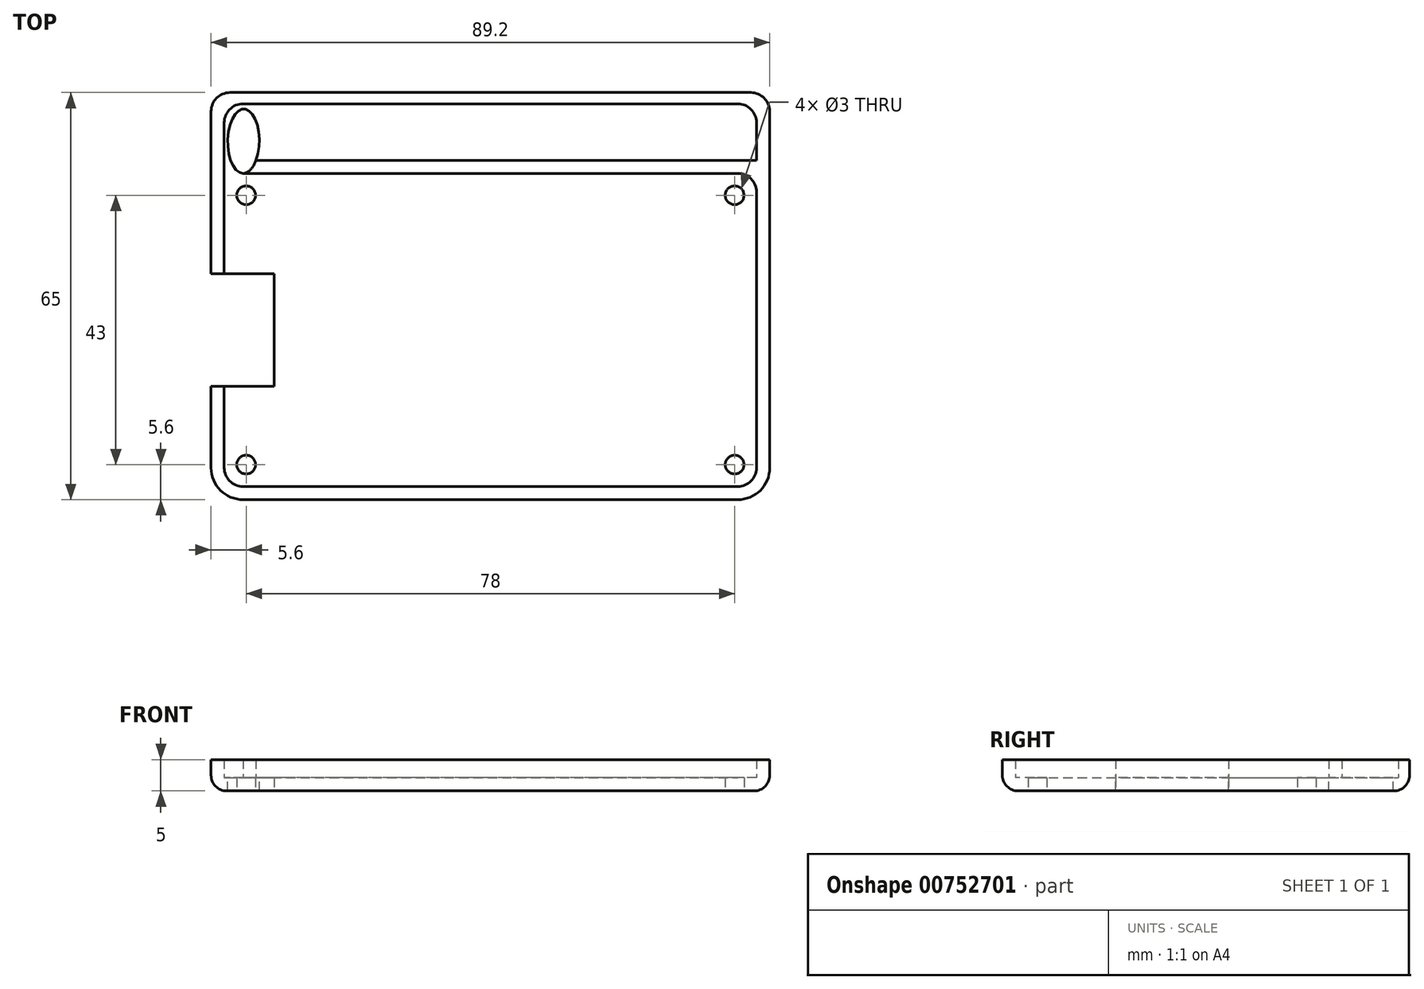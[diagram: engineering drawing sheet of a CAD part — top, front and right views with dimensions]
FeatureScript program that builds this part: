
annotation { "Feature Type Name" : "Feature", "Feature Type Description" : "" }
export const myFeature = defineFeature(function(context is Context, id is Id, definition is map)
    precondition{}
    {
        {
            var Q0;
            Q0=qCreatedBy(makeId("Top.planeOp"),FACE);
            var sketch = newSketch(context, id + "F0", { "sketchPlane" : qUnion([Q0])});
            skLineSegment(sketch, "E0.bottom", {"start": v(-39.5, 25) * mm, "end": v(39.5, 25) * mm});
            skLineSegment(sketch, "E0.top", {"start": v(-39.5, -25) * mm, "end": v(39.5, -25) * mm});
            skLineSegment(sketch, "E0.left", {"start": v(-42.5, 22) * mm, "end": v(-42.5, -22) * mm});
            skLineSegment(sketch, "E0.right", {"start": v(42.5, 22) * mm, "end": v(42.5, -22) * mm});
            skPoint(sketch, "E0.middle", {"position": v(0, 0) * mm});
            skLineSegment(sketch, "E1.bottom", {"start": v(-39, 21.5) * mm, "end": v(39, 21.5) * mm, "construction": true});
            skLineSegment(sketch, "E1.top", {"start": v(-39, -21.5) * mm, "end": v(39, -21.5) * mm, "construction": true});
            skLineSegment(sketch, "E1.left", {"start": v(-39, 21.5) * mm, "end": v(-39, -21.5) * mm, "construction": true});
            skLineSegment(sketch, "E1.right", {"start": v(39, 21.5) * mm, "end": v(39, -21.5) * mm, "construction": true});
            skCircle(sketch, "E2", {"center": v(-39, 21.5) * mm, "radius": 1.5 * mm});
            skCircle(sketch, "E3", {"center": v(39, 21.5) * mm, "radius": 1.5 * mm});
            skCircle(sketch, "E4", {"center": v(39, -21.5) * mm, "radius": 1.5 * mm});
            skCircle(sketch, "E5", {"center": v(-39, -21.5) * mm, "radius": 1.5 * mm});
            skPoint(sketch, "E6.visualSharp", {"position": v(-42.5, 25) * mm});
            skArc(sketch, "E6.filletArc", {"start": v(-39.5, 25) * mm, "mid": v(-41.62, 24.12) * mm, "end": v(-42.5, 22) * mm});
            skPoint(sketch, "E7.visualSharp", {"position": v(42.5, 25) * mm});
            skArc(sketch, "E7.filletArc", {"start": v(42.5, 22) * mm, "mid": v(41.62, 24.12) * mm, "end": v(39.5, 25) * mm});
            skPoint(sketch, "E8.visualSharp", {"position": v(42.5, -25) * mm});
            skArc(sketch, "E8.filletArc", {"start": v(39.5, -25) * mm, "mid": v(41.62, -24.12) * mm, "end": v(42.5, -22) * mm});
            skPoint(sketch, "E9.visualSharp", {"position": v(-42.5, -25) * mm});
            skArc(sketch, "E9.filletArc", {"start": v(-42.5, -22) * mm, "mid": v(-41.62, -24.12) * mm, "end": v(-39.5, -25) * mm});
            skLineSegment(sketch, "E10", {"start": v(0, 0) * mm, "end": v(-34.5, 0) * mm, "construction": true});
            skLineSegment(sketch, "E11", {"start": v(-34.5, 25) * mm, "end": v(-34.5, -25) * mm});
            skLineSegment(sketch, "E12", {"start": v(0, 0) * mm, "end": v(0, 9.32) * mm, "construction": true});
            skLineSegment(sketch, "E13.MirrorCS", {"start": v(34.5, 25) * mm, "end": v(34.5, -25) * mm});
            skLineSegment(sketch, "E14.1", {"start": v(-44.6, 22) * mm, "end": v(-44.6, -22) * mm});
            skLineSegment(sketch, "E14.2", {"start": v(-39.5, 27.1) * mm, "end": v(39.5, 27.1) * mm});
            skArc(sketch, "E14.3", {"start": v(-44.6, -22) * mm, "mid": v(-43.1, -25.6) * mm, "end": v(-39.5, -27.1) * mm});
            skLineSegment(sketch, "E14.5", {"start": v(44.6, 22) * mm, "end": v(44.6, -22) * mm});
            skArc(sketch, "E14.6", {"start": v(39.5, -27.1) * mm, "mid": v(43.1, -25.6) * mm, "end": v(44.6, -22) * mm});
            skLineSegment(sketch, "E14.7", {"start": v(-39.5, -27.1) * mm, "end": v(39.5, -27.1) * mm});
            skLineSegment(sketch, "E15", {"start": v(-42.5, 0) * mm, "end": v(-44.6, 0) * mm, "construction": true});
            skLineSegment(sketch, "E16.bottom", {"start": v(-44.6, 9) * mm, "end": v(-42.5, 9) * mm});
            skLineSegment(sketch, "E16.top", {"start": v(-44.6, -9) * mm, "end": v(-42.5, -9) * mm});
            skLineSegment(sketch, "E16.left", {"start": v(-44.6, 9) * mm, "end": v(-44.6, -9) * mm});
            skLineSegment(sketch, "E16.right", {"start": v(-42.5, 9) * mm, "end": v(-42.5, -9) * mm});
            skPoint(sketch, "E16.middle", {"position": v(-43.55, 0) * mm});
            skLineSegment(sketch, "E17", {"start": v(-42.5, 9) * mm, "end": v(-34.5, 9) * mm});
            skLineSegment(sketch, "E18", {"start": v(-42.5, -9) * mm, "end": v(-34.5, -9) * mm});
            skLineSegment(sketch, "E19", {"start": v(0, 27.1) * mm, "end": v(0, 36.1) * mm, "construction": true});
            skLineSegment(sketch, "E20", {"start": v(0, 36.1) * mm, "end": v(-39.5, 36.1) * mm});
            skLineSegment(sketch, "E21", {"start": v(0, 36.1) * mm, "end": v(39.5, 36.1) * mm});
            skLineSegment(sketch, "E22.0", {"start": v(0, 37.9) * mm, "end": v(41.6, 37.9) * mm});
            skLineSegment(sketch, "E22.1", {"start": v(0, 37.9) * mm, "end": v(-41.6, 37.9) * mm});
            skLineSegment(sketch, "E23", {"start": v(-42.5, 22) * mm, "end": v(-42.5, 33.1) * mm});
            skLineSegment(sketch, "E24", {"start": v(42.5, 22) * mm, "end": v(42.5, 33.1) * mm});
            skPoint(sketch, "E25.visualSharp", {"position": v(42.5, 36.1) * mm});
            skArc(sketch, "E25.filletArc", {"start": v(42.5, 33.1) * mm, "mid": v(41.62, 35.22) * mm, "end": v(39.5, 36.1) * mm});
            skPoint(sketch, "E26.visualSharp", {"position": v(-42.5, 36.1) * mm});
            skArc(sketch, "E26.filletArc", {"start": v(-39.5, 36.1) * mm, "mid": v(-41.62, 35.22) * mm, "end": v(-42.5, 33.1) * mm});
            skPoint(sketch, "E27.start.orphan", {"position": v(-44.6, 36.1) * mm});
            skPoint(sketch, "E28.start.orphan", {"position": v(44.6, 36.1) * mm});
            skLineSegment(sketch, "E29", {"start": v(-44.6, 22) * mm, "end": v(-44.6, 34.9) * mm});
            skLineSegment(sketch, "E30", {"start": v(44.6, 22) * mm, "end": v(44.6, 34.9) * mm});
            skPoint(sketch, "E31.visualSharp", {"position": v(-44.6, 37.9) * mm});
            skArc(sketch, "E31.filletArc", {"start": v(-41.6, 37.9) * mm, "mid": v(-43.72, 37.02) * mm, "end": v(-44.6, 34.9) * mm});
            skPoint(sketch, "E32.visualSharp", {"position": v(44.6, 37.9) * mm});
            skArc(sketch, "E32.filletArc", {"start": v(44.6, 34.9) * mm, "mid": v(43.72, 37.02) * mm, "end": v(41.6, 37.9) * mm});
            skLineSegment(sketch, "E33", {"start": v(-39.5, 27.1) * mm, "end": v(-42.5, 27.1) * mm});
            skLineSegment(sketch, "E34", {"start": v(39.5, 27.1) * mm, "end": v(42.5, 27.1) * mm});
            skEllipse(sketch, "E35", {"center": v(-39.42, 30.14) * mm, "majorRadius": 5.14 * mm, "minorRadius": 2.52 * mm, "majorAxis": v(-0.02, -1)});
            skSolve(sketch);
        }
        {
            var Q0;
            Q0=makeQuery(id+"F0.imprint","IMPRINT",FACE,{"disambiguationData":[TD([[makeQuery(id+"F0.imprint","IMPRINT",EDGE,{"derivedFrom":sQuery(id+"F0.wireOp",EDGE,"E0.right")}),1.0]])]});
            var Q1;
            Q1=makeQuery(id+"F0.imprint","IMPRINT",FACE,{"disambiguationData":[TD([[makeQuery(id+"F0.imprint","IMPRINT",EDGE,{"derivedFrom":sQuery(id+"F0.wireOp",EDGE,"E2")}),-1.0]])]});
            var Q2;
            Q2=makeQuery(id+"F0.imprint","IMPRINT",FACE,{"disambiguationData":[TD([[makeQuery(id+"F0.imprint","IMPRINT",EDGE,{"derivedFrom":sQuery(id+"F0.wireOp",EDGE,"E5")}),-1.0]])]});
            var Q3;
            {var subQ7=sQuery(id+"F0.wireOp",EDGE,"E13.MirrorCS");Q3=makeQuery(id+"F0.imprint","IMPRINT",FACE,{"disambiguationData":[TD([[makeQuery(id+"F0.imprint","IMPRINT",EDGE,{"derivedFrom":subQ7}),-1.0]])]});}
            var Q4;
            Q4=makeQuery(id+"F0.imprint","IMPRINT",FACE,{"disambiguationData":[TD([[makeQuery(id+"F0.imprint","IMPRINT",EDGE,{"derivedFrom":sQuery(id+"F0.wireOp",EDGE,"E0.right")}),-1.0]])]});
            var Q5;
            {var subQ0=sQuery(id+"F0.wireOp",EDGE,"E6.filletArc");Q5=makeQuery(id+"F0.imprint","IMPRINT",FACE,{"disambiguationData":[TD([[makeQuery(id+"F0.imprint","IMPRINT",EDGE,{"derivedFrom":subQ0}),-1.0]])]});}
            var Q6;
            Q6=makeQuery(id+"F0.imprint","IMPRINT",FACE,{"disambiguationData":[TD([[makeQuery(id+"F0.imprint","IMPRINT",EDGE,{"derivedFrom":sQuery(id+"F0.wireOp",EDGE,"E20")}),1.0]])]});
            var Q7;
            {var subQ0=sQuery(id+"F0.wireOp",EDGE,"E7.filletArc");Q7=makeQuery(id+"F0.imprint","IMPRINT",FACE,{"disambiguationData":[TD([[makeQuery(id+"F0.imprint","IMPRINT",EDGE,{"derivedFrom":subQ0}),-1.0]])]});}
            extrude(context, id + "F1", {"entities" : qUnion([Q0, Q1, Q2, Q3, Q4, Q5, Q6, Q7]), "depth" : 2.1 * mm, "offsetDistance" : 25 * mm});
        }
        {
            var Q0;
            Q0=makeQuery(id+"F0.imprint","IMPRINT",FACE,{"disambiguationData":[TD([[makeQuery(id+"F0.imprint","IMPRINT",EDGE,{"derivedFrom":sQuery(id+"F0.wireOp",EDGE,"E0.right")}),1.0]])]});
            var Q1;
            {var subQ0=sQuery(id+"F0.wireOp",EDGE,"E7.filletArc");Q1=makeQuery(id+"F0.imprint","IMPRINT",FACE,{"disambiguationData":[TD([[makeQuery(id+"F0.imprint","IMPRINT",EDGE,{"derivedFrom":subQ0}),-1.0]])]});}
            extrude(context, id + "F2", {"entities" : qUnion([Q0, Q1]), "operationType" : NewBodyOperationType.ADD, "depth" : 5 * mm, "offsetDistance" : 25 * mm});
        }
        {
            var Q0;
            Q0=makeQuery(id+"F1.opExtrude","CAP_EDGE",EDGE,{"disambiguationData":[OSD([sQuery(id+"F0.wireOp",EDGE,"E14.5"),sQuery(id+"F0.wireOp",EDGE,"E30")])],"isStart":true});
            fillet(context, id + "F3", {"entities" : qUnion([Q0]), "radius" : 2.5 * mm, "tangentPropagation" : true, "allowEdgeOverflow" : false});
        }
    });
